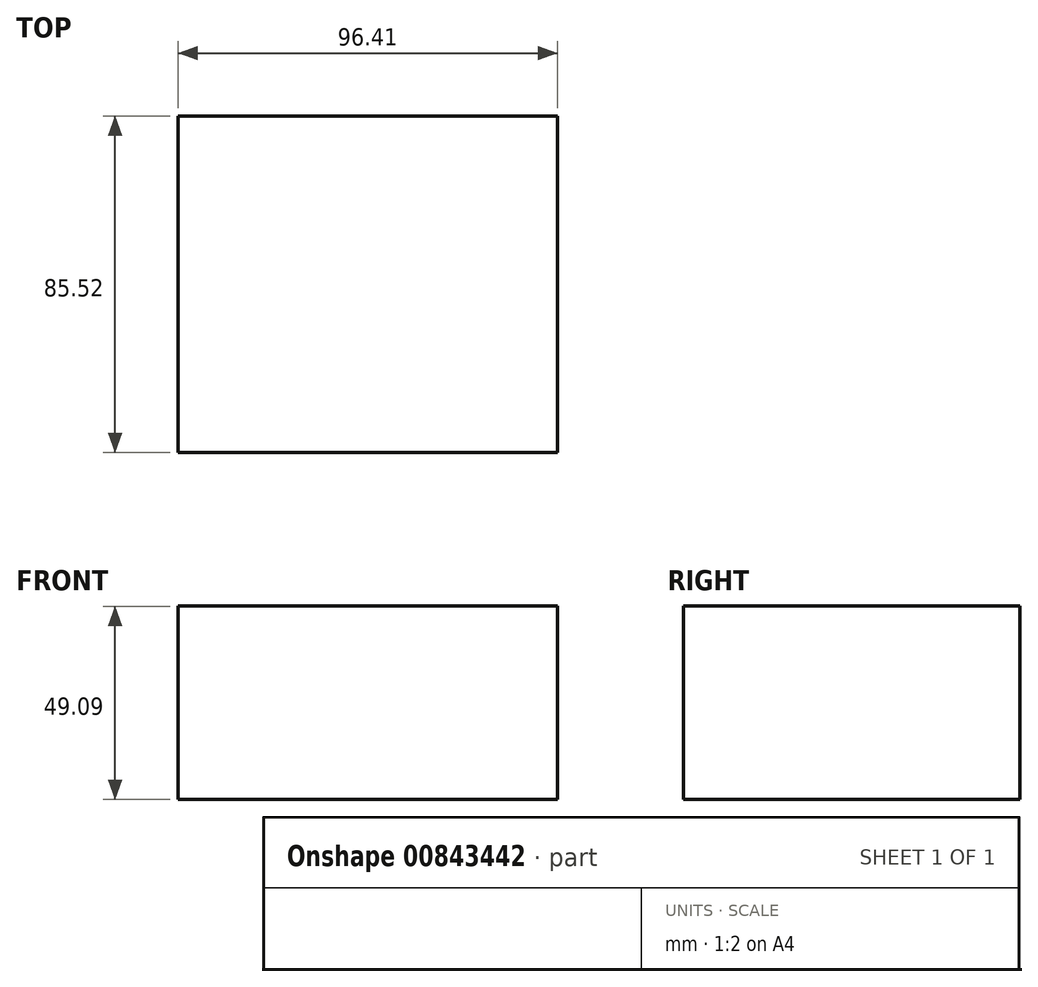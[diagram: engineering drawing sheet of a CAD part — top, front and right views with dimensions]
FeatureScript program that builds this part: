
annotation { "Feature Type Name" : "Feature", "Feature Type Description" : "" }
export const myFeature = defineFeature(function(context is Context, id is Id, definition is map)
    precondition{}
    {
        {
            var Q0;
            Q0=qCreatedBy(makeId("Front.planeOp"),FACE);
            var sketch = newSketch(context, id + "F0", { "sketchPlane" : qUnion([Q0])});
            skLineSegment(sketch, "E0.bottom", {"start": v(47.85, -16.12) * mm, "end": v(-48.56, -16.12) * mm});
            skLineSegment(sketch, "E0.top", {"start": v(47.85, 32.97) * mm, "end": v(-48.56, 32.97) * mm});
            skLineSegment(sketch, "E0.left", {"start": v(47.85, -16.12) * mm, "end": v(47.85, 32.97) * mm});
            skLineSegment(sketch, "E0.right", {"start": v(-48.56, -16.12) * mm, "end": v(-48.56, 32.97) * mm});
            skSolve(sketch);
        }
        {
            var Q0;
            Q0 = qSketchRegion(id + "F0", true);
            extrude(context, id + "F1", {"entities" : qUnion([Q0]), "depth" : 85.52 * mm, "offsetDistance" : 25.4 * mm});
        }
    });
